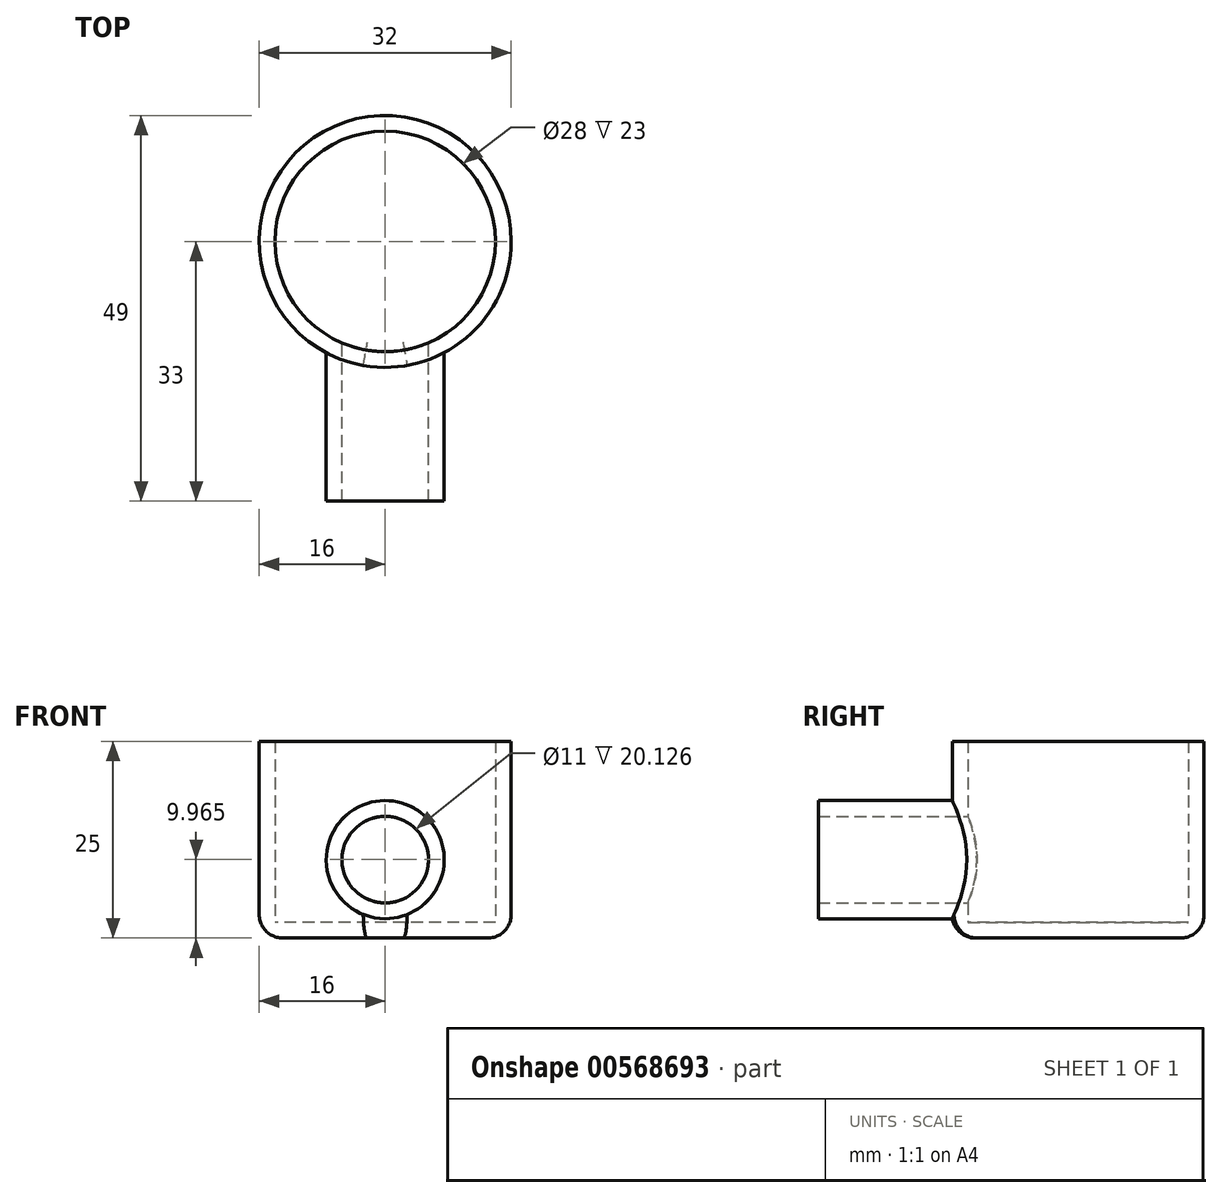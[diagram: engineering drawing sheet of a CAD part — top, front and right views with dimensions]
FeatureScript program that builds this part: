
annotation { "Feature Type Name" : "Feature", "Feature Type Description" : "" }
export const myFeature = defineFeature(function(context is Context, id is Id, definition is map)
    precondition{}
    {
        {
            var Q0;
            Q0=qCreatedBy(makeId("Top.planeOp"),FACE);
            var sketch = newSketch(context, id + "F0", { "sketchPlane" : qUnion([Q0])});
            skCircle(sketch, "E0", {"center": v(0, 0) * mm, "radius": 16 * mm});
            skSolve(sketch);
        }
        {
            var Q0;
            Q0=makeQuery(id+"F0.imprint","IMPRINT",FACE,{"disambiguationData":[TD([[makeQuery(id+"F0.imprint","IMPRINT",EDGE,{"derivedFrom":sQuery(id+"F0.wireOp",EDGE,"E0")}),1.0]])]});
            extrude(context, id + "F1", {"entities" : qUnion([Q0]), "depth" : 25 * mm, "offsetDistance" : 25 * mm});
        }
        {
            var Q0;
            Q0=qCreatedBy(makeId("Front.planeOp"),FACE);
            cPlane(context, id + "F2", {"entities" : qUnion([Q0]), "cplaneType" : CPlaneType.OFFSET, "offset" : 13 * mm, "width" : 150 * mm, "height" : 150 * mm});
        }
        {
            var Q0;
            Q0=qCreatedBy(id+"F2.planeOp",FACE);
            var sketch = newSketch(context, id + "F3", { "sketchPlane" : qUnion([Q0])});
            skCircle(sketch, "E1", {"center": v(0, 9.96) * mm, "radius": 7.5 * mm});
            skSolve(sketch);
        }
        {
            var Q0;
            Q0 = qSketchRegion(id + "F3", true);
            extrude(context, id + "F4", {"entities" : qUnion([Q0]), "operationType" : NewBodyOperationType.ADD, "depth" : 20 * mm, "offsetDistance" : 25 * mm});
        }
        {
            var Q0;
            Q0=makeQuery(id+"F1.opExtrude","CAP_FACE",FACE,{"disambiguationData":[OSD([sQuery(id+"F0.wireOp",EDGE,"E0")])],"isStart":false});
            var Q1;
            Q1=makeQuery(id+"F4.opExtrude","CAP_FACE",FACE,{"disambiguationData":[OSD([sQuery(id+"F3.wireOp",EDGE,"E1")])],"isStart":false});
            shell(context, id + "F5", {"entities" : qUnion([Q0, Q1]), "thickness" : 2 * mm});
        }
        {
            var Q0;
            Q0=makeQuery(id+"F1.opExtrude","CAP_EDGE",EDGE,{"disambiguationData":[OSD([sQuery(id+"F0.wireOp",EDGE,"E0")])],"isStart":true});
            fillet(context, id + "F6", {"entities" : qUnion([Q0]), "radius" : 3 * mm, "tangentPropagation" : true, "allowEdgeOverflow" : false});
        }
    });
